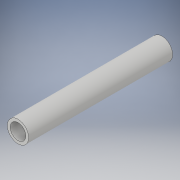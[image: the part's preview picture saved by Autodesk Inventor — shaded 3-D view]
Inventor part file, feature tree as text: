
AUTODESK INVENTOR PART (.ipt)
format: ipt  version: 2019 (Build 230136000, 136)  size: 98,304 bytes
history: native  units: mm
features: extrude x2, sketch x2
ambient origin geometry x8: Origin, YZ Plane, XZ Plane, XY Plane, X Axis, Y Axis, Z Axis, Center Point
bodies: Solid1 (feature_tree)
feature tree (4):
  extrude  "Extrusion1"  Depth=101.264mm TaperAngle=0.0deg
  extrude  "Extrusion2"  Depth=101.264mm TaperAngle=0.0deg
  sketch  "Sketch1"  dims[d0=15.0mm d1=101.264mm d2=0.0mm]
  sketch  "Sketch2"  dims[d3=11.0mm d4=101.264mm d5=0.0mm]
